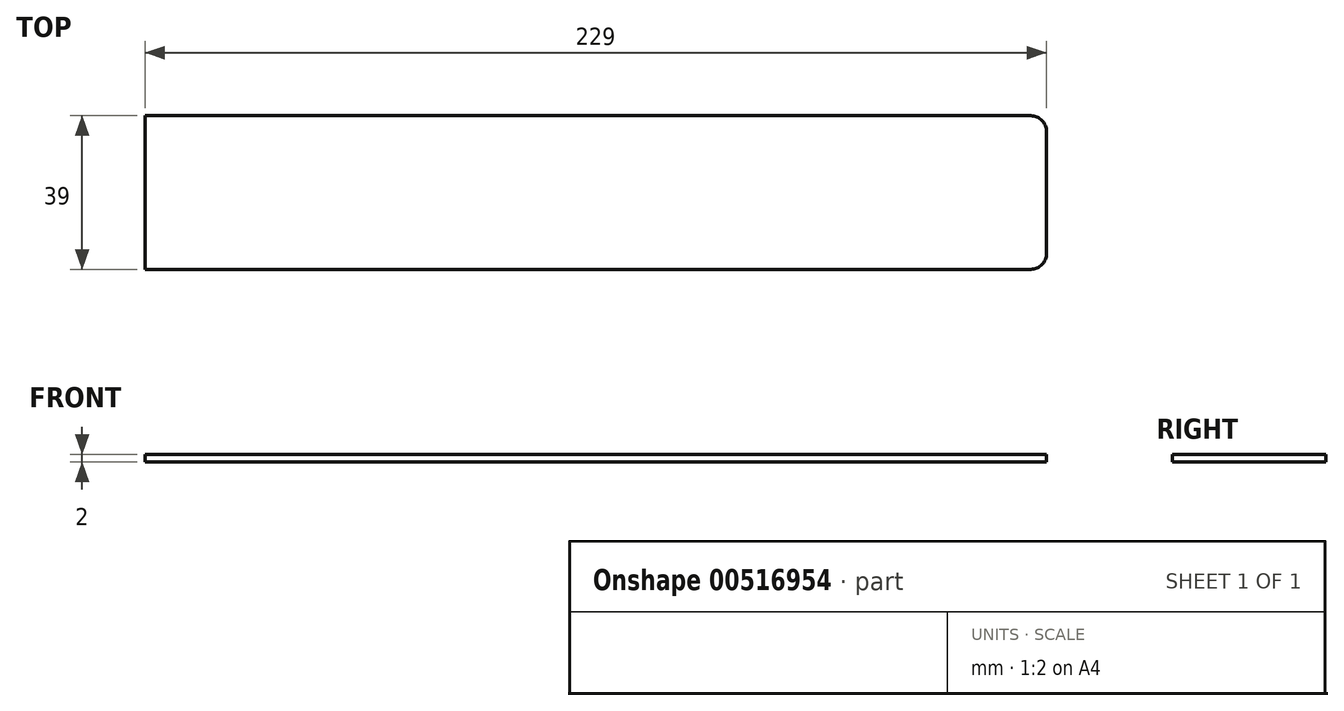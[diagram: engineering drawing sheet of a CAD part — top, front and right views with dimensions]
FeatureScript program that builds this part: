
annotation { "Feature Type Name" : "Feature", "Feature Type Description" : "" }
export const myFeature = defineFeature(function(context is Context, id is Id, definition is map)
    precondition{}
    {
        {
            var Q0;
            Q0=qCreatedBy(makeId("Top.planeOp"),FACE);
            var sketch = newSketch(context, id + "F0", { "sketchPlane" : qUnion([Q0])});
            skLineSegment(sketch, "E0.bottom", {"start": v(110.5, 19.5) * mm, "end": v(-114.5, 19.5) * mm});
            skLineSegment(sketch, "E0.top", {"start": v(110.5, -19.5) * mm, "end": v(-114.5, -19.5) * mm});
            skLineSegment(sketch, "E0.left", {"start": v(114.5, 15.5) * mm, "end": v(114.5, -15.5) * mm});
            skLineSegment(sketch, "E0.right", {"start": v(-114.5, 19.5) * mm, "end": v(-114.5, -19.5) * mm});
            skPoint(sketch, "E0.middle", {"position": v(0, 0) * mm});
            skPoint(sketch, "E1.visualSharp", {"position": v(114.5, -19.5) * mm});
            skArc(sketch, "E1.filletArc", {"start": v(110.5, -19.5) * mm, "mid": v(113.33, -18.33) * mm, "end": v(114.5, -15.5) * mm});
            skPoint(sketch, "E2.visualSharp", {"position": v(114.5, 19.5) * mm});
            skArc(sketch, "E2.filletArc", {"start": v(114.5, 15.5) * mm, "mid": v(113.33, 18.33) * mm, "end": v(110.5, 19.5) * mm});
            skSolve(sketch);
        }
        {
            var Q0;
            Q0=makeQuery(id+"F0.imprint","IMPRINT",FACE,{"disambiguationData":[TD([[makeQuery(id+"F0.imprint","IMPRINT",EDGE,{"derivedFrom":sQuery(id+"F0.wireOp",EDGE,"E0.bottom")}),1.0]])]});
            extrude(context, id + "F1", {"entities" : qUnion([Q0]), "depth" : 2 * mm, "offsetDistance" : 25 * mm});
        }
    });
